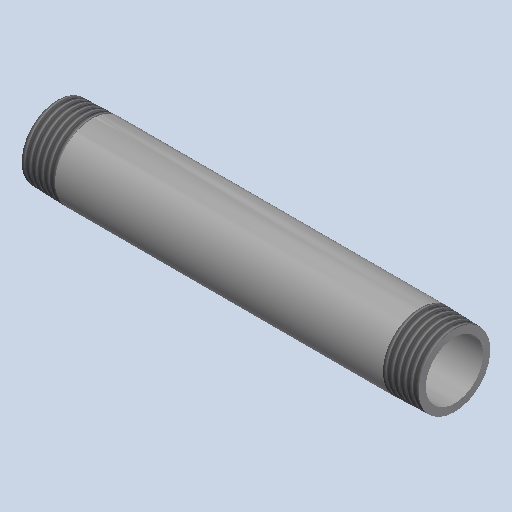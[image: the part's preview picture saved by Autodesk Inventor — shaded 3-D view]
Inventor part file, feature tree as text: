
AUTODESK INVENTOR PART (.ipt)
format: ipt  version: 2025 (Build 290162000, 162)  size: 204,800 bytes
history: native  units: mm (DEFAULTED — no unit token found)
features: other x8, revolve x1
ambient origin geometry x8: Origin, YZ Plane, XZ Plane, XY Plane, X Axis, Y Axis, Z Axis, Center Point
bodies: Solid1 (feature_tree)
feature tree (9):
  revolve  "Revolution1"  [1 undecoded]
  other  "Work Axis1"
  other  "Work Point5"
  other  "Work Axis2"
  other  "Work Point6"
  other  "Work Axis3"
  other  "Work Axis4"
  other  "Work Point7"
  other  "Work Point8"
note: 1 required parameter value undecoded (feature->parameter linkage not recoverable at this tier; creation-order binding heuristic only, values carry confidence <= 0.55)
